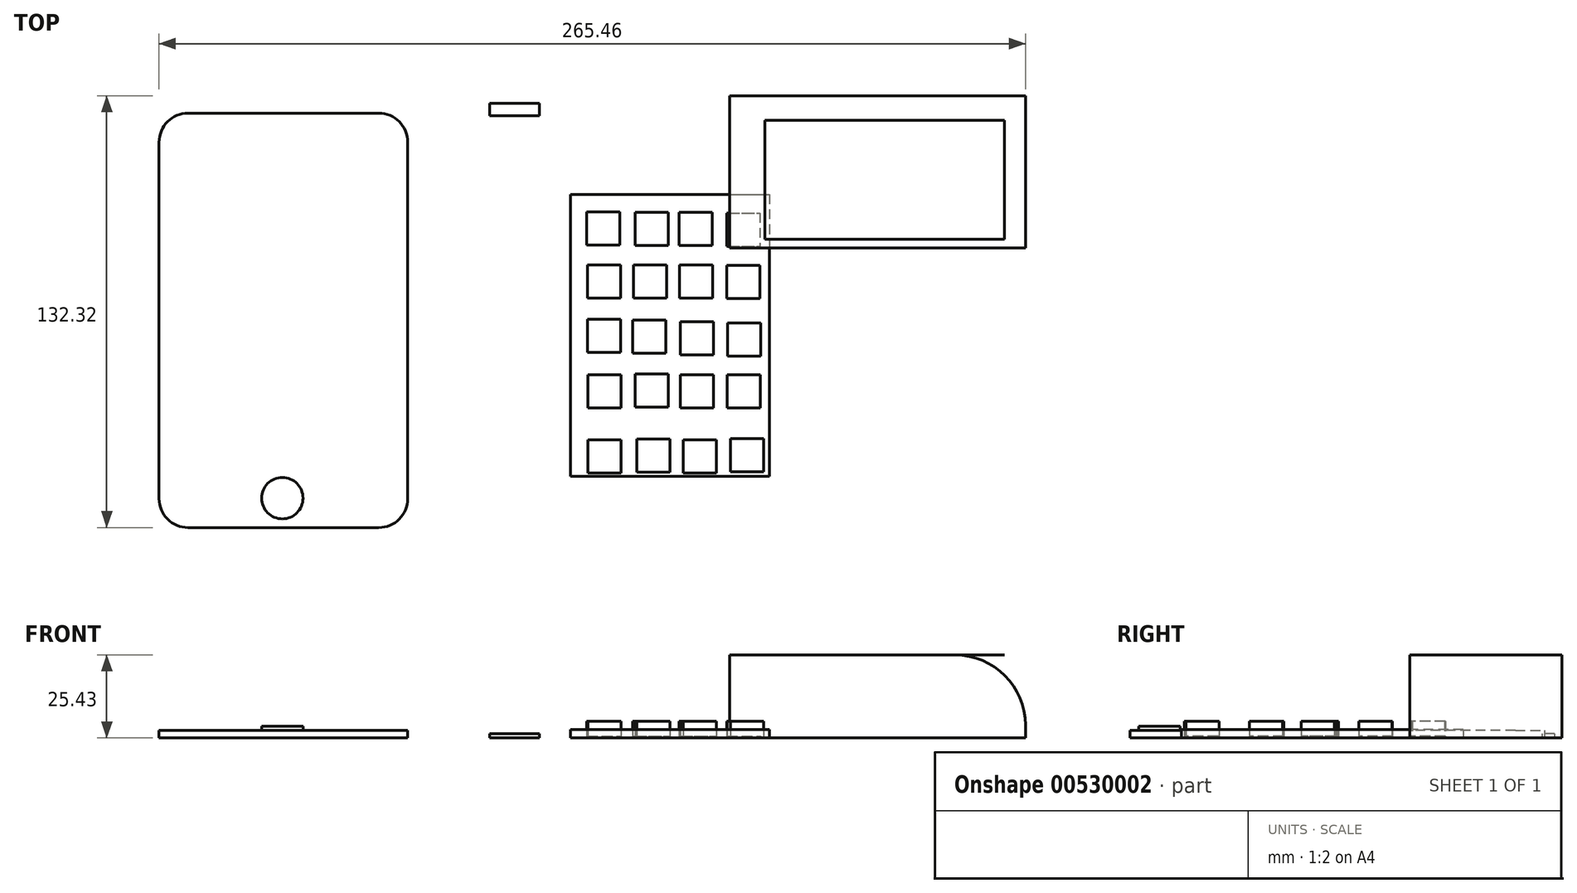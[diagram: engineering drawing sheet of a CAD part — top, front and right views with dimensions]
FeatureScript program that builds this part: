
annotation { "Feature Type Name" : "Feature", "Feature Type Description" : "" }
export const myFeature = defineFeature(function(context is Context, id is Id, definition is map)
    precondition{}
    {
        {
            var Q0;
            Q0=qCreatedBy(makeId("Top.planeOp"),FACE);
            var sketch = newSketch(context, id + "F0", { "sketchPlane" : qUnion([Q0])});
            skLineSegment(sketch, "E0.bottom", {"start": v(-30.48, 43.18) * mm, "end": v(30.48, 43.18) * mm});
            skLineSegment(sketch, "E0.top", {"start": v(-30.48, -43.18) * mm, "end": v(30.48, -43.18) * mm});
            skLineSegment(sketch, "E0.left", {"start": v(-30.48, 43.18) * mm, "end": v(-30.48, -43.18) * mm});
            skLineSegment(sketch, "E0.right", {"start": v(30.48, 43.18) * mm, "end": v(30.48, -43.18) * mm});
            skPoint(sketch, "E0.middle", {"position": v(0, 0) * mm});
            skPoint(sketch, "E1", {"position": v(0, 43.18) * mm});
            skPoint(sketch, "E2", {"position": v(-20.45, 31.93) * mm});
            skPoint(sketch, "E3", {"position": v(-5.17, 31.93) * mm});
            skPoint(sketch, "E4", {"position": v(8.84, 31.93) * mm});
            skPoint(sketch, "E5", {"position": v(23.17, 31.93) * mm});
            skSolve(sketch);
        }
        {
            var Q0;
            Q0=makeQuery(id+"F0.imprint","IMPRINT",FACE,{"disambiguationData":[TD([[makeQuery(id+"F0.imprint","IMPRINT",EDGE,{"derivedFrom":sQuery(id+"F0.wireOp",EDGE,"E0.bottom")}),-1.0]])]});
            var sketch = newSketch(context, id + "F1", { "sketchPlane" : qUnion([Q0])});
            skLineSegment(sketch, "E6.bottom", {"start": v(17.4, 21.42) * mm, "end": v(27.57, 21.42) * mm});
            skLineSegment(sketch, "E6.top", {"start": v(17.4, 11.26) * mm, "end": v(27.57, 11.26) * mm});
            skLineSegment(sketch, "E6.left", {"start": v(17.4, 21.42) * mm, "end": v(17.4, 11.26) * mm});
            skLineSegment(sketch, "E6.right", {"start": v(27.57, 21.42) * mm, "end": v(27.57, 11.26) * mm});
            skLineSegment(sketch, "E7.bottom", {"start": v(3.07, -12.13) * mm, "end": v(13.23, -12.13) * mm});
            skLineSegment(sketch, "E7.top", {"start": v(3.07, -22.3) * mm, "end": v(13.23, -22.3) * mm});
            skLineSegment(sketch, "E7.left", {"start": v(3.07, -12.13) * mm, "end": v(3.07, -22.3) * mm});
            skLineSegment(sketch, "E7.right", {"start": v(13.23, -12.13) * mm, "end": v(13.23, -22.3) * mm});
            skLineSegment(sketch, "E8.bottom", {"start": v(17.5, -12.13) * mm, "end": v(27.67, -12.13) * mm});
            skLineSegment(sketch, "E8.top", {"start": v(17.5, -22.3) * mm, "end": v(27.67, -22.3) * mm});
            skLineSegment(sketch, "E8.left", {"start": v(17.5, -12.13) * mm, "end": v(17.5, -22.3) * mm});
            skLineSegment(sketch, "E8.right", {"start": v(27.67, -12.13) * mm, "end": v(27.67, -22.3) * mm});
            skLineSegment(sketch, "E9.bottom", {"start": v(4, -32.1) * mm, "end": v(14.15, -32.1) * mm});
            skLineSegment(sketch, "E9.top", {"start": v(4, -42.26) * mm, "end": v(14.15, -42.26) * mm});
            skLineSegment(sketch, "E9.left", {"start": v(4, -32.1) * mm, "end": v(4, -42.26) * mm});
            skLineSegment(sketch, "E9.right", {"start": v(14.15, -32.1) * mm, "end": v(14.15, -42.26) * mm});
            skLineSegment(sketch, "E10.bottom", {"start": v(-25.57, 37.74) * mm, "end": v(-15.4, 37.74) * mm});
            skLineSegment(sketch, "E10.top", {"start": v(-25.57, 27.58) * mm, "end": v(-15.4, 27.58) * mm});
            skLineSegment(sketch, "E10.left", {"start": v(-25.57, 37.74) * mm, "end": v(-25.57, 27.58) * mm});
            skLineSegment(sketch, "E10.right", {"start": v(-15.4, 37.74) * mm, "end": v(-15.4, 27.58) * mm});
            skLineSegment(sketch, "E11.bottom", {"start": v(-11.53, 4.62) * mm, "end": v(-1.37, 4.62) * mm});
            skLineSegment(sketch, "E11.top", {"start": v(-11.53, -5.54) * mm, "end": v(-1.37, -5.54) * mm});
            skLineSegment(sketch, "E11.left", {"start": v(-11.53, 4.62) * mm, "end": v(-11.53, -5.54) * mm});
            skLineSegment(sketch, "E11.right", {"start": v(-1.37, 4.62) * mm, "end": v(-1.37, -5.54) * mm});
            skLineSegment(sketch, "E12.bottom", {"start": v(-25.35, 4.93) * mm, "end": v(-15.2, 4.93) * mm});
            skLineSegment(sketch, "E12.top", {"start": v(-25.35, -5.23) * mm, "end": v(-15.2, -5.23) * mm});
            skLineSegment(sketch, "E12.left", {"start": v(-25.35, 4.93) * mm, "end": v(-25.35, -5.23) * mm});
            skLineSegment(sketch, "E12.right", {"start": v(-15.2, 4.93) * mm, "end": v(-15.2, -5.23) * mm});
            skLineSegment(sketch, "E13.bottom", {"start": v(-11.22, 21.51) * mm, "end": v(-1.06, 21.51) * mm});
            skLineSegment(sketch, "E13.top", {"start": v(-11.22, 11.35) * mm, "end": v(-1.06, 11.35) * mm});
            skLineSegment(sketch, "E13.left", {"start": v(-11.22, 21.51) * mm, "end": v(-11.22, 11.35) * mm});
            skLineSegment(sketch, "E13.right", {"start": v(-1.06, 21.51) * mm, "end": v(-1.06, 11.35) * mm});
            skLineSegment(sketch, "E14.bottom", {"start": v(2.76, 37.62) * mm, "end": v(12.92, 37.62) * mm});
            skLineSegment(sketch, "E14.top", {"start": v(2.76, 27.46) * mm, "end": v(12.92, 27.46) * mm});
            skLineSegment(sketch, "E14.left", {"start": v(2.76, 37.62) * mm, "end": v(2.76, 27.46) * mm});
            skLineSegment(sketch, "E14.right", {"start": v(12.92, 37.62) * mm, "end": v(12.92, 27.46) * mm});
            skLineSegment(sketch, "E15.bottom", {"start": v(-10.75, 37.62) * mm, "end": v(-0.59, 37.62) * mm});
            skLineSegment(sketch, "E15.top", {"start": v(-10.75, 27.46) * mm, "end": v(-0.59, 27.46) * mm});
            skLineSegment(sketch, "E15.left", {"start": v(-10.75, 37.62) * mm, "end": v(-10.75, 27.46) * mm});
            skLineSegment(sketch, "E15.right", {"start": v(-0.59, 37.62) * mm, "end": v(-0.59, 27.46) * mm});
            skLineSegment(sketch, "E16.bottom", {"start": v(-25.35, 21.51) * mm, "end": v(-15.2, 21.51) * mm});
            skLineSegment(sketch, "E16.top", {"start": v(-25.35, 11.35) * mm, "end": v(-15.2, 11.35) * mm});
            skLineSegment(sketch, "E16.left", {"start": v(-25.35, 21.51) * mm, "end": v(-25.35, 11.35) * mm});
            skLineSegment(sketch, "E16.right", {"start": v(-15.2, 21.51) * mm, "end": v(-15.2, 11.35) * mm});
            skLineSegment(sketch, "E17.bottom", {"start": v(2.86, 21.52) * mm, "end": v(13.02, 21.52) * mm});
            skLineSegment(sketch, "E17.top", {"start": v(2.86, 11.36) * mm, "end": v(13.02, 11.36) * mm});
            skLineSegment(sketch, "E17.left", {"start": v(2.86, 21.52) * mm, "end": v(2.86, 11.36) * mm});
            skLineSegment(sketch, "E17.right", {"start": v(13.02, 21.52) * mm, "end": v(13.02, 11.36) * mm});
            skLineSegment(sketch, "E18.bottom", {"start": v(17.34, 37.48) * mm, "end": v(27.5, 37.48) * mm});
            skLineSegment(sketch, "E18.top", {"start": v(17.34, 27.32) * mm, "end": v(27.5, 27.32) * mm});
            skLineSegment(sketch, "E18.left", {"start": v(17.34, 37.48) * mm, "end": v(17.34, 27.32) * mm});
            skLineSegment(sketch, "E18.right", {"start": v(27.5, 37.48) * mm, "end": v(27.5, 27.32) * mm});
            skLineSegment(sketch, "E19.bottom", {"start": v(3.07, 4.15) * mm, "end": v(13.23, 4.15) * mm});
            skLineSegment(sketch, "E19.top", {"start": v(3.07, -6.01) * mm, "end": v(13.23, -6.01) * mm});
            skLineSegment(sketch, "E19.left", {"start": v(3.07, 4.15) * mm, "end": v(3.07, -6.01) * mm});
            skLineSegment(sketch, "E19.right", {"start": v(13.23, 4.15) * mm, "end": v(13.23, -6.01) * mm});
            skLineSegment(sketch, "E20.bottom", {"start": v(17.65, 3.74) * mm, "end": v(27.8, 3.74) * mm});
            skLineSegment(sketch, "E20.top", {"start": v(17.65, -6.42) * mm, "end": v(27.8, -6.42) * mm});
            skLineSegment(sketch, "E20.left", {"start": v(17.65, 3.74) * mm, "end": v(17.65, -6.42) * mm});
            skLineSegment(sketch, "E20.right", {"start": v(27.8, 3.74) * mm, "end": v(27.8, -6.42) * mm});
            skLineSegment(sketch, "E21.bottom", {"start": v(-25.19, -12.13) * mm, "end": v(-15.03, -12.13) * mm});
            skLineSegment(sketch, "E21.top", {"start": v(-25.19, -22.3) * mm, "end": v(-15.03, -22.3) * mm});
            skLineSegment(sketch, "E21.left", {"start": v(-25.19, -12.13) * mm, "end": v(-25.19, -22.3) * mm});
            skLineSegment(sketch, "E21.right", {"start": v(-15.03, -12.13) * mm, "end": v(-15.03, -22.3) * mm});
            skLineSegment(sketch, "E22.bottom", {"start": v(-25.2, -32.1) * mm, "end": v(-15.05, -32.1) * mm});
            skLineSegment(sketch, "E22.top", {"start": v(-25.2, -42.26) * mm, "end": v(-15.05, -42.26) * mm});
            skLineSegment(sketch, "E22.left", {"start": v(-25.2, -32.1) * mm, "end": v(-25.2, -42.26) * mm});
            skLineSegment(sketch, "E22.right", {"start": v(-15.05, -32.1) * mm, "end": v(-15.05, -42.26) * mm});
            skLineSegment(sketch, "E23.bottom", {"start": v(-10.16, -31.79) * mm, "end": v(0, -31.79) * mm});
            skLineSegment(sketch, "E23.top", {"start": v(-10.16, -41.95) * mm, "end": v(0, -41.95) * mm});
            skLineSegment(sketch, "E23.left", {"start": v(-10.16, -31.79) * mm, "end": v(-10.16, -41.95) * mm});
            skLineSegment(sketch, "E23.right", {"start": v(0, -31.79) * mm, "end": v(0, -41.95) * mm});
            skLineSegment(sketch, "E24.bottom", {"start": v(-10.75, -11.82) * mm, "end": v(-0.59, -11.82) * mm});
            skLineSegment(sketch, "E24.top", {"start": v(-10.75, -21.98) * mm, "end": v(-0.59, -21.98) * mm});
            skLineSegment(sketch, "E24.left", {"start": v(-10.75, -11.82) * mm, "end": v(-10.75, -21.98) * mm});
            skLineSegment(sketch, "E24.right", {"start": v(-0.59, -11.82) * mm, "end": v(-0.59, -21.98) * mm});
            skLineSegment(sketch, "E25.bottom", {"start": v(18.5, -31.62) * mm, "end": v(28.66, -31.62) * mm});
            skLineSegment(sketch, "E25.top", {"start": v(18.5, -41.78) * mm, "end": v(28.66, -41.78) * mm});
            skLineSegment(sketch, "E25.left", {"start": v(18.5, -31.62) * mm, "end": v(18.5, -41.78) * mm});
            skLineSegment(sketch, "E25.right", {"start": v(28.66, -31.62) * mm, "end": v(28.66, -41.78) * mm});
            skSolve(sketch);
        }
        {
            var Q0;
            Q0=makeQuery(id+"F1.imprint","IMPRINT",FACE,{"disambiguationData":[TD([[makeQuery(id+"F1.imprint","IMPRINT",EDGE,{"derivedFrom":sQuery(id+"F1.wireOp",EDGE,"E17.bottom")}),-1.0]])]});
            var Q1;
            Q1=makeQuery(id+"F1.imprint","IMPRINT",FACE,{"disambiguationData":[TD([[makeQuery(id+"F1.imprint","IMPRINT",EDGE,{"derivedFrom":sQuery(id+"F1.wireOp",EDGE,"E16.bottom")}),-1.0]])]});
            var Q2;
            Q2=makeQuery(id+"F1.imprint","IMPRINT",FACE,{"disambiguationData":[TD([[makeQuery(id+"F1.imprint","IMPRINT",EDGE,{"derivedFrom":sQuery(id+"F1.wireOp",EDGE,"E10.bottom")}),-1.0]])]});
            var Q3;
            Q3=makeQuery(id+"F1.imprint","IMPRINT",FACE,{"disambiguationData":[TD([[makeQuery(id+"F1.imprint","IMPRINT",EDGE,{"derivedFrom":sQuery(id+"F1.wireOp",EDGE,"E15.bottom")}),-1.0]])]});
            var Q4;
            {var subQ5=sQuery(id+"F1.wireOp",EDGE,"E14.left");Q4=makeQuery(id+"F1.imprint","IMPRINT",FACE,{"disambiguationData":[TD([[makeQuery(id+"F1.imprint","IMPRINT",EDGE,{"derivedFrom":subQ5}),1.0]])]});}
            var Q5;
            {var subQ2=sQuery(id+"F1.wireOp",EDGE,"E12.top");Q5=makeQuery(id+"F1.imprint","IMPRINT",FACE,{"disambiguationData":[TD([[makeQuery(id+"F1.imprint","IMPRINT",EDGE,{"derivedFrom":subQ2}),1.0]])]});}
            var Q6;
            {var subQ1=sQuery(id+"F1.wireOp",EDGE,"E6.bottom");Q6=makeQuery(id+"F1.imprint","IMPRINT",FACE,{"disambiguationData":[TD([[makeQuery(id+"F1.imprint","IMPRINT",EDGE,{"derivedFrom":subQ1}),-1.0]])]});}
            var Q7;
            Q7=makeQuery(id+"F1.imprint","IMPRINT",FACE,{"disambiguationData":[TD([[makeQuery(id+"F1.imprint","IMPRINT",EDGE,{"derivedFrom":sQuery(id+"F1.wireOp",EDGE,"E11.bottom")}),-1.0]])]});
            var Q8;
            Q8=makeQuery(id+"F1.imprint","IMPRINT",FACE,{"disambiguationData":[TD([[makeQuery(id+"F1.imprint","IMPRINT",EDGE,{"derivedFrom":sQuery(id+"F1.wireOp",EDGE,"E7.bottom")}),-1.0]])]});
            var Q9;
            Q9=makeQuery(id+"F1.imprint","IMPRINT",FACE,{"disambiguationData":[TD([[makeQuery(id+"F1.imprint","IMPRINT",EDGE,{"derivedFrom":sQuery(id+"F1.wireOp",EDGE,"E8.bottom")}),-1.0]])]});
            var Q10;
            Q10=makeQuery(id+"F1.imprint","IMPRINT",FACE,{"disambiguationData":[TD([[makeQuery(id+"F1.imprint","IMPRINT",EDGE,{"derivedFrom":sQuery(id+"F1.wireOp",EDGE,"E9.bottom")}),-1.0]])]});
            var Q11;
            Q11=makeQuery(id+"F1.imprint","IMPRINT",FACE,{"disambiguationData":[TD([[makeQuery(id+"F1.imprint","IMPRINT",EDGE,{"derivedFrom":sQuery(id+"F1.wireOp",EDGE,"E13.bottom")}),-1.0]])]});
            var Q12;
            Q12=makeQuery(id+"F1.imprint","IMPRINT",FACE,{"disambiguationData":[TD([[makeQuery(id+"F1.imprint","IMPRINT",EDGE,{"derivedFrom":sQuery(id+"F1.wireOp",EDGE,"E18.bottom")}),-1.0]])]});
            var Q13;
            Q13=makeQuery(id+"F1.imprint","IMPRINT",FACE,{"disambiguationData":[TD([[makeQuery(id+"F1.imprint","IMPRINT",EDGE,{"derivedFrom":sQuery(id+"F1.wireOp",EDGE,"c4cdf0d2-04cc-4c49-ab98-41cd47113664.bottom")}),-1.0]])]});
            var Q14;
            Q14=makeQuery(id+"F1.imprint","IMPRINT",FACE,{"disambiguationData":[TD([[makeQuery(id+"F1.imprint","IMPRINT",EDGE,{"derivedFrom":sQuery(id+"F1.wireOp",EDGE,"E19.bottom")}),-1.0]])]});
            var Q15;
            Q15=makeQuery(id+"F1.imprint","IMPRINT",FACE,{"disambiguationData":[TD([[makeQuery(id+"F1.imprint","IMPRINT",EDGE,{"derivedFrom":sQuery(id+"F1.wireOp",EDGE,"E20.bottom")}),-1.0]])]});
            var Q16;
            Q16=makeQuery(id+"F1.imprint","IMPRINT",FACE,{"disambiguationData":[TD([[makeQuery(id+"F1.imprint","IMPRINT",EDGE,{"derivedFrom":sQuery(id+"F1.wireOp",EDGE,"c4cdf0d2-04cc-4c49-ab98-41cd47113664.bottom")}),-1.0]])]});
            var Q17;
            Q17=makeQuery(id+"F1.imprint","IMPRINT",FACE,{"disambiguationData":[TD([[makeQuery(id+"F1.imprint","IMPRINT",EDGE,{"derivedFrom":sQuery(id+"F1.wireOp",EDGE,"E24.bottom")}),-1.0]])]});
            var Q18;
            Q18=makeQuery(id+"F1.imprint","IMPRINT",FACE,{"disambiguationData":[TD([[makeQuery(id+"F1.imprint","IMPRINT",EDGE,{"derivedFrom":sQuery(id+"F1.wireOp",EDGE,"E23.bottom")}),-1.0]])]});
            var Q19;
            Q19=makeQuery(id+"F1.imprint","IMPRINT",FACE,{"disambiguationData":[TD([[makeQuery(id+"F1.imprint","IMPRINT",EDGE,{"derivedFrom":sQuery(id+"F1.wireOp",EDGE,"E22.bottom")}),-1.0]])]});
            var Q20;
            Q20=makeQuery(id+"F1.imprint","IMPRINT",FACE,{"disambiguationData":[TD([[makeQuery(id+"F1.imprint","IMPRINT",EDGE,{"derivedFrom":sQuery(id+"F1.wireOp",EDGE,"E21.bottom")}),-1.0]])]});
            extrude(context, id + "F2", {"entities" : qUnion([Q0, Q1, Q2, Q3, Q4, Q5, Q6, Q7, Q8, Q9, Q10, Q11, Q12, Q13, Q14, Q15, Q16, Q17, Q18, Q19, Q20]), "depth" : 0.5 * mm, "offsetDistance" : 25.4 * mm});
        }
        {
            var Q0;
            Q0=qCreatedBy(makeId("Top.planeOp"),FACE);
            var sketch = newSketch(context, id + "F3", { "sketchPlane" : qUnion([Q0])});
            skLineSegment(sketch, "E26.bottom", {"start": v(-147.7, 68.05) * mm, "end": v(-89.27, 68.05) * mm});
            skLineSegment(sketch, "E26.top", {"start": v(-147.7, -58.95) * mm, "end": v(-89.27, -58.95) * mm});
            skLineSegment(sketch, "E26.left", {"start": v(-156.58, 59.16) * mm, "end": v(-156.58, -50.06) * mm});
            skLineSegment(sketch, "E26.right", {"start": v(-80.38, 59.16) * mm, "end": v(-80.38, -50.06) * mm});
            skPoint(sketch, "E26.middle", {"position": v(-118.48, 4.55) * mm});
            skPoint(sketch, "E27", {"position": v(-118.48, -49.58) * mm});
            skPoint(sketch, "E28.visualSharp", {"position": v(-156.58, -58.95) * mm});
            skArc(sketch, "E28.filletArc", {"start": v(-156.58, -50.06) * mm, "mid": v(-153.98, -56.34) * mm, "end": v(-147.7, -58.95) * mm});
            skPoint(sketch, "E29.visualSharp", {"position": v(-80.38, -58.95) * mm});
            skArc(sketch, "E29.filletArc", {"start": v(-89.27, -58.95) * mm, "mid": v(-82.99, -56.34) * mm, "end": v(-80.38, -50.06) * mm});
            skPoint(sketch, "E30.visualSharp", {"position": v(-80.38, 68.05) * mm});
            skArc(sketch, "E30.filletArc", {"start": v(-80.38, 59.16) * mm, "mid": v(-82.99, 65.45) * mm, "end": v(-89.27, 68.05) * mm});
            skPoint(sketch, "E31.visualSharp", {"position": v(-156.58, 68.05) * mm});
            skArc(sketch, "E31.filletArc", {"start": v(-147.7, 68.05) * mm, "mid": v(-153.98, 65.45) * mm, "end": v(-156.58, 59.16) * mm});
            skSolve(sketch);
        }
        {
            var Q0;
            Q0 = qSketchRegion(id + "F3", true);
            extrude(context, id + "F4", {"entities" : qUnion([Q0]), "depth" : 2.3 * mm, "offsetDistance" : 25.4 * mm});
        }
        {
            var Q0;
            Q0=makeQuery(id+"F0.imprint","IMPRINT",FACE,{"disambiguationData":[TD([[makeQuery(id+"F0.imprint","IMPRINT",EDGE,{"derivedFrom":sQuery(id+"F0.wireOp",EDGE,"E0.bottom")}),-1.0]])]});
            extrude(context, id + "F5", {"entities" : qUnion([Q0]), "depth" : 2.54 * mm, "offsetDistance" : 25.4 * mm});
        }
        {
            var Q0;
            Q0=makeQuery(id+"F4.opExtrude","CAP_FACE",FACE,{"disambiguationData":[OSD([sQuery(id+"F3.wireOp",EDGE,"E26.bottom"),sQuery(id+"F3.wireOp",EDGE,"E26.top"),sQuery(id+"F3.wireOp",EDGE,"E26.left"),sQuery(id+"F3.wireOp",EDGE,"E26.right"),sQuery(id+"F3.wireOp",EDGE,"E28.filletArc"),sQuery(id+"F3.wireOp",EDGE,"E29.filletArc"),sQuery(id+"F3.wireOp",EDGE,"E30.filletArc"),sQuery(id+"F3.wireOp",EDGE,"E31.filletArc")])],"isStart":false});
            var sketch = newSketch(context, id + "F6", { "sketchPlane" : qUnion([Q0])});
            skCircle(sketch, "E32", {"center": v(-118.82, -49.91) * mm, "radius": 6.35 * mm});
            skSolve(sketch);
        }
        {
            var Q0;
            Q0=makeQuery(id+"F6.imprint","IMPRINT",FACE,{"disambiguationData":[TD([[makeQuery(id+"F6.imprint","IMPRINT",EDGE,{"derivedFrom":sQuery(id+"F6.wireOp",EDGE,"E32")}),1.0]])]});
            extrude(context, id + "F7", {"entities" : qUnion([Q0]), "operationType" : NewBodyOperationType.ADD, "depth" : 1.27 * mm, "offsetDistance" : 25.4 * mm});
        }
        {
            var Q0;
            Q0 = qSketchRegion(id + "F1", true);
            extrude(context, id + "F8", {"entities" : qUnion([Q0]), "depth" : 5.08 * mm, "offsetDistance" : 25.4 * mm});
        }
        {
            var Q0;
            Q0=qCreatedBy(makeId("Top.planeOp"),FACE);
            var sketch = newSketch(context, id + "F9", { "sketchPlane" : qUnion([Q0])});
            skLineSegment(sketch, "E33.bottom", {"start": v(-55.3, 71.1) * mm, "end": v(-40.07, 71.1) * mm});
            skLineSegment(sketch, "E33.top", {"start": v(-55.3, 67.28) * mm, "end": v(-40.07, 67.28) * mm});
            skLineSegment(sketch, "E33.left", {"start": v(-55.3, 71.1) * mm, "end": v(-55.3, 67.28) * mm});
            skLineSegment(sketch, "E33.right", {"start": v(-40.07, 71.1) * mm, "end": v(-40.07, 67.28) * mm});
            skPoint(sketch, "E33.middle", {"position": v(-47.69, 69.19) * mm});
            skSolve(sketch);
        }
        {
            var Q0;
            Q0=makeQuery(id+"F9.imprint","IMPRINT",FACE,{"disambiguationData":[TD([[makeQuery(id+"F9.imprint","IMPRINT",EDGE,{"derivedFrom":sQuery(id+"F9.wireOp",EDGE,"E33.bottom")}),-1.0]])]});
            extrude(context, id + "F10", {"entities" : qUnion([Q0]), "depth" : 1.27 * mm, "offsetDistance" : 25.4 * mm});
        }
        {
            var Q0;
            Q0=qCreatedBy(makeId("Top.planeOp"),FACE);
            var sketch = newSketch(context, id + "F11", { "sketchPlane" : qUnion([Q0])});
            skLineSegment(sketch, "E34.bottom", {"start": v(108.88, 26.79) * mm, "end": v(18.27, 26.79) * mm});
            skLineSegment(sketch, "E34.top", {"start": v(108.88, 73.37) * mm, "end": v(18.27, 73.37) * mm});
            skLineSegment(sketch, "E34.left", {"start": v(108.88, 26.79) * mm, "end": v(108.88, 73.37) * mm});
            skLineSegment(sketch, "E34.right", {"start": v(18.27, 26.79) * mm, "end": v(18.27, 73.37) * mm});
            skPoint(sketch, "E34.middle", {"position": v(63.58, 50.08) * mm});
            skSolve(sketch);
        }
        {
            var Q0;
            Q0 = qSketchRegion(id + "F11", true);
            extrude(context, id + "F12", {"entities" : qUnion([Q0]), "depth" : 25.4 * mm, "offsetDistance" : 25.4 * mm});
        }
        {
            var Q0;
            Q0=makeQuery(id+"F12.opExtrude","CAP_FACE",FACE,{"disambiguationData":[OSD([sQuery(id+"F11.wireOp",EDGE,"E34.bottom"),sQuery(id+"F11.wireOp",EDGE,"E34.top"),sQuery(id+"F11.wireOp",EDGE,"E34.left"),sQuery(id+"F11.wireOp",EDGE,"E34.right")])],"isStart":false});
            var sketch = newSketch(context, id + "F13", { "sketchPlane" : qUnion([Q0])});
            skLineSegment(sketch, "E35.bottom", {"start": v(28.98, 65.9) * mm, "end": v(102.45, 65.9) * mm});
            skLineSegment(sketch, "E35.top", {"start": v(28.98, 29.39) * mm, "end": v(102.45, 29.39) * mm});
            skLineSegment(sketch, "E35.left", {"start": v(28.98, 65.9) * mm, "end": v(28.98, 29.39) * mm});
            skLineSegment(sketch, "E35.right", {"start": v(102.45, 65.9) * mm, "end": v(102.45, 29.39) * mm});
            skSolve(sketch);
        }
        {
            var Q0;
            Q0=makeQuery(id+"F13.imprint","IMPRINT",FACE,{"disambiguationData":[TD([[makeQuery(id+"F13.imprint","IMPRINT",EDGE,{"derivedFrom":sQuery(id+"F13.wireOp",EDGE,"E35.bottom")}),-1.0]])]});
            extrude(context, id + "F14", {"entities" : qUnion([Q0]), "depth" : 0.03 * mm, "offsetDistance" : 25.4 * mm});
        }
        {
            var Q0;
            Q0=makeQuery(id+"F12.opExtrude","CAP_EDGE",EDGE,{"disambiguationData":[OSD([sQuery(id+"F11.wireOp",EDGE,"E34.left")])],"isStart":false});
            fillet(context, id + "F15", {"entities" : qUnion([Q0]), "radius" : 21.46 * mm, "tangentPropagation" : true, "allowEdgeOverflow" : false});
        }
    });
